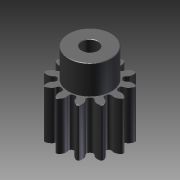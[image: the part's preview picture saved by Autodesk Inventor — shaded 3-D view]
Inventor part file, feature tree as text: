
AUTODESK INVENTOR PART (.ipt)
format: ipt  version: 2011 SP1 (Build 150282100, 282)  size: 419,840 bytes
history: native  units: mm
features: other x14, revolve x3, sketch x3, extrude x1, hole x1
ambient origin geometry x8: Origin, YZ Plane, XZ Plane, XY Plane, X Axis, Y Axis, Z Axis, Center Point
bodies: Solid1 (feature_tree)
feature tree (22):
  revolve  "Revolution1"  [1 undecoded]
  extrude  "Extrusion1"  TaperAngle=360.0deg  [1 undecoded]
  hole  "Hole1"  [1 undecoded]
  revolve  "Revolution2"  [1 undecoded]
  revolve  "Revolution3"  [1 undecoded]
  other  "b_XY"
  other  "b_YZ"
  other  "b_ZX"
  other  "b_X"
  other  "b_Y"
  other  "b_Z"
  other  "b_Center"
  other  "turn_around_XY"
  other  "turn_around_YZ"
  other  "turn_around_ZX"
  other  "turn_around_X"
  other  "turn_around_Y"
  other  "turn_around_Z"
  other  "turn_around_Center"
  sketch  "Sketch_2"  dims[d0=360.0deg d1=30.0mm d2=0.0mm]
  sketch  "Sketch_3"  dims[d3=10.0mm d4=6.0mm d5=4.0mm d6=2.0mm d7=90.0deg d8=48.0mm d9=0.0mm d10=360.0deg]
  sketch  "Sketch3"  dims[d11=360.0deg d12=0.0mm]
note: 5 required parameter values undecoded (feature->parameter linkage not recoverable at this tier; creation-order binding heuristic only, values carry confidence <= 0.55)